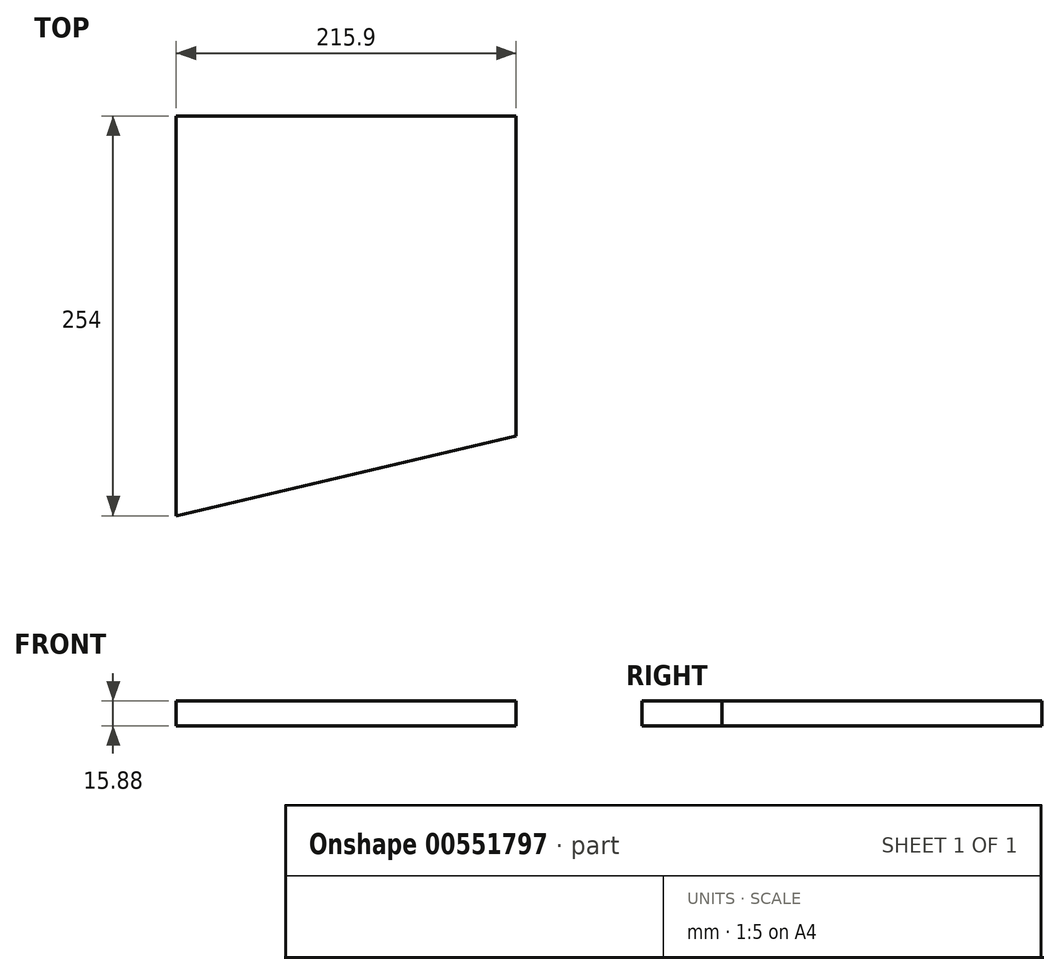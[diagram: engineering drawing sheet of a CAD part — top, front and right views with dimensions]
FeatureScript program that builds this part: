
annotation { "Feature Type Name" : "Feature", "Feature Type Description" : "" }
export const myFeature = defineFeature(function(context is Context, id is Id, definition is map)
    precondition{}
    {
        {
            var Q0;
            Q0=qCreatedBy(makeId("Top.planeOp"),FACE);
            var sketch = newSketch(context, id + "F0", { "sketchPlane" : qUnion([Q0])});
            skLineSegment(sketch, "E0.bottom", {"start": v(-132.9, 190.24) * mm, "end": v(83, 190.24) * mm});
            skLineSegment(sketch, "E0.top", {"start": v(-132.9, -63.76) * mm, "end": v(83, -63.76) * mm});
            skLineSegment(sketch, "E0.left", {"start": v(-132.9, 190.24) * mm, "end": v(-132.9, -63.76) * mm});
            skLineSegment(sketch, "E0.right", {"start": v(83, 190.24) * mm, "end": v(83, -63.76) * mm});
            skPoint(sketch, "E1", {"position": v(83, -12.96) * mm});
            skLineSegment(sketch, "E2", {"start": v(-132.9, -63.76) * mm, "end": v(83, -12.96) * mm});
            skSolve(sketch);
        }
        {
            var Q0;
            {var subQ0=sQuery(id+"F0.wireOp",EDGE,"E0.bottom");Q0=makeQuery(id+"F0.imprint","IMPRINT",FACE,{"disambiguationData":[TD([[makeQuery(id+"F0.imprint","IMPRINT",EDGE,{"derivedFrom":subQ0}),-1.0]])]});}
            extrude(context, id + "F1", {"entities" : qUnion([Q0]), "depth" : 15.88 * mm, "offsetDistance" : 25.4 * mm});
        }
    });
